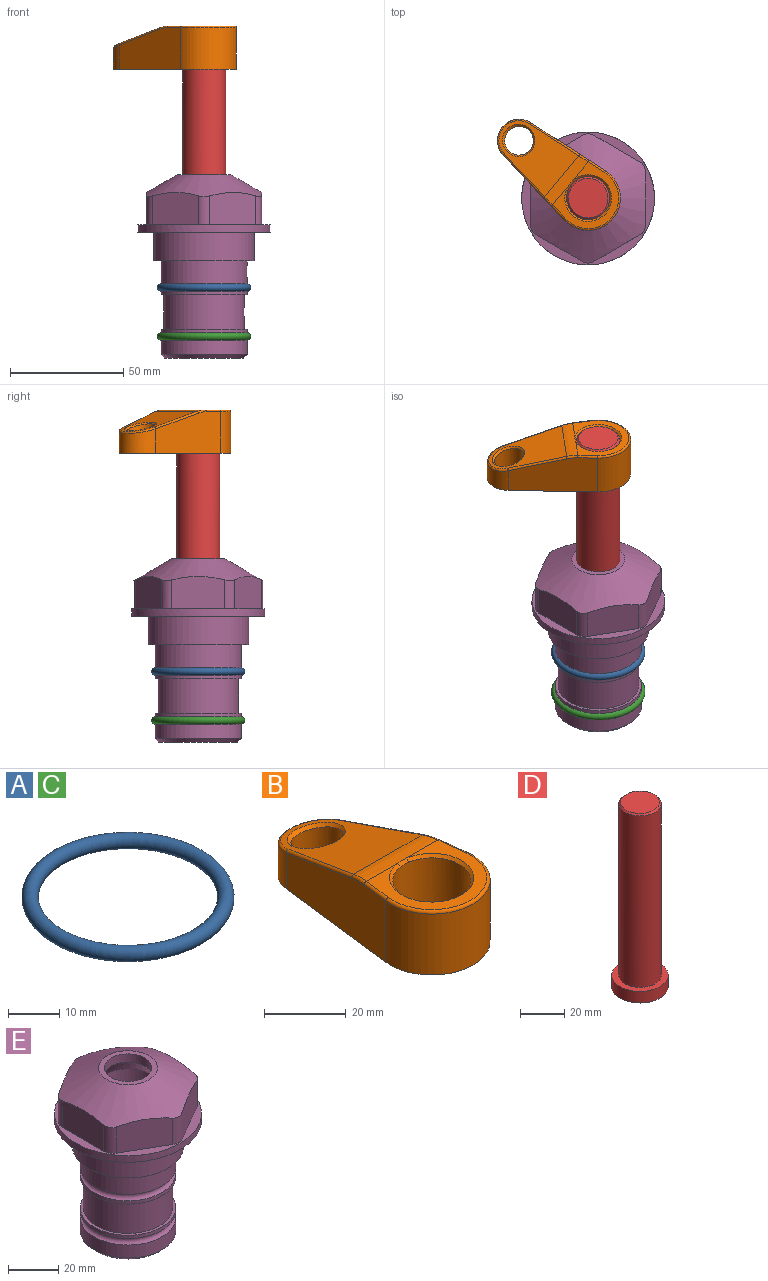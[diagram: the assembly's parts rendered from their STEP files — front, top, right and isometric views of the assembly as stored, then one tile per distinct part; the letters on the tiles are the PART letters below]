
ASSEMBLY  parts=5 mates=4
PART A: 1 faces, bbox 44.7x44.7x3.2 mm
  f0: torus R=19.05mm, axis (0,0,1), area 1193.9mm2
PART B: 31 faces, bbox 31.7x65.5x19.8 mm
  f0: plane 39.12x18.26mm, normal (0.99,0.12,0), area 612.2mm2, adj f1,f4,f7,f11,f13,f15
  f1: cylinder r=9.53mm len=18.91mm, axis (0,0,-1), area 296.1mm2, adj f0,f2,f7,f17
  f2: plane 39.12x18.26mm, normal (-0.99,0.12,0), area 612.2mm2, adj f1,f4,f7,f12,f14,f16
  f3: cylinder r=6.35mm len=12.7mm, axis (0,0,-1), area 362.4mm2, adj f7,f18
  f4: cylinder r=14.29mm len=28.58mm, axis (0,0,-1), area 882.2mm2, adj f0,f2,f7,f10
  f5: cylinder r=9.53mm len=19.05mm, axis (0,0,-1), area 1092.6mm2, adj f7,f19,f20
  f6: plane 26.99x23.69mm, normal (0,0,1), area 216.2mm2, adj f9,f10,f11,f12,f19
  f7: plane 63.5x28.58mm, normal (0,0,-1), area 661.8mm2, adj f0,f1,f2,f3,f4,f5,f22,f23
  f8: plane 33.52x23.6mm, normal (0,0.26,0.97), area 486mm2, adj f9,f15,f16,f17,f18
  f9: cylinder r=19.05mm len=24.72mm, axis (1,0,0), area 120.4mm2, adj f6,f8,f13,f14,f20
  f10: torus R=13.49mm, axis (0,0,1), area 59mm2, adj f4,f6,f11,f12
  f11: cylinder r=0.79mm len=8.67mm, axis (0.12,-0.99,0), area 10.8mm2, adj f0,f6,f10,f13
  f12: cylinder r=0.79mm len=8.67mm, axis (0.12,0.99,0), area 10.8mm2, adj f2,f6,f10,f14
  f13: bspline ~4.95x1.42mm, area 6.1mm2, adj f0,f9,f11,f15
  f14: bspline ~4.95x1.42mm, area 6.1mm2, adj f2,f9,f12,f16
  f15: cylinder r=0.79mm len=25.95mm, axis (0.12,-0.96,0.26), area 32.9mm2, adj f0,f8,f13,f17
  f16: cylinder r=0.79mm len=25.95mm, axis (0.12,0.96,-0.26), area 32.9mm2, adj f2,f8,f14,f17
  f17: bspline ~18.91x8.38mm, area 30mm2, adj f1,f8,f15,f16
  f18: bspline ~14.29x14.29mm, area 48.3mm2, adj f3,f8
  f19: cone r=9.53mm half-angle=45deg, axis (0,0,1), area 66.5mm2, adj f5,f6,f20
  f20: bspline ~3.22x0.96mm, area 3.5mm2, adj f5,f9,f19
  f21: plane 2.75x2.72mm, normal (0,0,-1), area 2.9mm2, adj f23,f25,f28
  f22: plane 23.05x15.88mm, normal (-0.99,-0.12,0), area 323.6mm2, adj f7,f25,f26,f27,f28,f29
  f23: plane 23.05x15.88mm, normal (0.99,-0.12,0), area 323.6mm2, adj f7,f21,f25,f27,f28,f30
  f24: cylinder r=9.53mm len=10.69mm, axis (0,0,-1), area 114.7mm2, adj f7,f27,f29,f30
  f25: cylinder r=12.7mm len=20.59mm, axis (0,0,-1), area 381.1mm2, adj f7,f21,f22,f23,f26,f28
  f26: plane 2.75x2.72mm, normal (0,0,-1), area 2.9mm2, adj f22,f25,f28
  f27: plane 19.72x18.37mm, normal (0,-0.26,-0.97), area 291.8mm2, adj f22,f23,f24,f28,f29,f30
  f28: cylinder r=15.88mm len=19.92mm, axis (1,0,0), area 54.8mm2, adj f21,f22,f23,f25,f26,f27
  f29: cylinder r=1.59mm len=11mm, axis (0,0,-1), area 34.7mm2, adj f7,f22,f24,f27
  f30: cylinder r=1.59mm len=11mm, axis (0,0,-1), area 34.7mm2, adj f7,f23,f24,f27
PART C: same geometry as A
PART D: 6 faces, bbox 25.4x25.4x101.6 mm
  f0: plane 17.46x17.46mm, normal (0,0,1), area 239.5mm2, adj f5
  f1: plane 25.4x25.4mm, normal (0,0,-1), area 506.7mm2, adj f2
  f2: cylinder r=12.7mm len=25.4mm, axis (0,0,1), area 506.7mm2, adj f1,f3
  f3: plane 25.4x25.4mm, normal (0,0,1), area 221.7mm2, adj f2,f4
  f4: cylinder r=9.53mm len=94.46mm, axis (0,0,1), area 5653mm2, adj f3,f5
  f5: cone r=8.73mm half-angle=45deg, axis (0,0,-1), area 64.4mm2, adj f0,f4
PART E: 36 faces, bbox 58.7x58.7x81 mm
  f0: cylinder r=17.78mm len=35.56mm, axis (0,0,1), area 1670.8mm2, adj f23,f24,f31
  f1: cylinder r=19.05mm len=38.1mm, axis (0,0,1), area 1191.9mm2, adj f26,f27,f30
  f2: plane 58.66x58.66mm, normal (0,0,-1), area 1150.6mm2, adj f3,f28
  f3: cylinder r=29.33mm len=58.66mm, axis (0,0,-1), area 585.1mm2, adj f2,f4
  f4: plane 58.66x58.66mm, normal (0,0,1), area 475.9mm2, adj f3,f5,f6,f7,f8,f9,f10,f11
  f5: plane 20.32x14.34mm, normal (-0.5,0.87,0), area 324.4mm2, adj f4,f15,f16,f17
  f6: plane 20.32x14.34mm, normal (0.5,0.87,0), area 324.4mm2, adj f4,f14,f15,f17
  f7: plane 23.48x14.34mm, normal (1,0,0), area 324.4mm2, adj f4,f13,f14,f17
  f8: plane 20.32x14.34mm, normal (0.5,-0.87,0), area 324.4mm2, adj f4,f12,f13,f17
  f9: plane 20.32x14.34mm, normal (-0.5,-0.87,0), area 324.4mm2, adj f4,f11,f12,f17
  f10: plane 23.48x14.34mm, normal (-1,0,0), area 324.4mm2, adj f4,f11,f16,f17
  f11: cylinder r=5.08mm len=12.85mm, axis (0,0,-1), area 67.2mm2, adj f4,f9,f10,f17
  f12: cylinder r=5.08mm len=12.85mm, axis (0,0,-1), area 67.2mm2, adj f4,f8,f9,f17
  f13: cylinder r=5.08mm len=12.85mm, axis (0,0,-1), area 67.2mm2, adj f4,f7,f8,f17
  f14: cylinder r=5.08mm len=12.85mm, axis (0,0,-1), area 67.2mm2, adj f4,f6,f7,f17
  f15: cylinder r=5.08mm len=12.85mm, axis (0,0,-1), area 67.2mm2, adj f4,f5,f6,f17
  f16: cylinder r=5.08mm len=12.85mm, axis (0,0,-1), area 67.2mm2, adj f4,f5,f10,f17
  f17: cone r=11.73mm half-angle=60deg, axis (0,0,-1), area 2071.8mm2, adj f5,f6,f7,f8,f9,f10,f11,f12
  f18: plane 23.46x23.46mm, normal (0,0,1), area 147.4mm2, adj f17,f35
  f19: plane 34.93x34.93mm, normal (0,0,-1), area 958mm2, adj f29
  f20: cylinder r=19.05mm len=38.1mm, axis (0,0,1), area 760.1mm2, adj f21,f29
  f21: torus R=19.05mm, axis (0,0,1), area 565.3mm2, adj f20,f22
  f22: cylinder r=19.05mm len=38.1mm, axis (0,0,1), area 190mm2, adj f21,f23
  f23: plane 38.1x38.1mm, normal (0,0,1), area 146.9mm2, adj f0,f22
  f24: plane 38.1x38.1mm, normal (0,0,-1), area 146.9mm2, adj f0,f25
  f25: cylinder r=19.05mm len=38.1mm, axis (0,0,1), area 190mm2, adj f24,f26
  f26: torus R=19.05mm, axis (0,0,1), area 565.3mm2, adj f1,f25
  f27: plane 44.45x44.45mm, normal (0,0,-1), area 411.7mm2, adj f1,f28
  f28: cylinder r=22.23mm len=44.45mm, axis (0,0,1), area 1773.5mm2, adj f2,f27
  f29: cone r=19.05mm half-angle=45deg, axis (0,0,1), area 257.5mm2, adj f19,f20
  f30: cylinder r=3.17mm len=6.75mm, axis (-1,0,0), area 128mm2, adj f1,f33
  f31: cylinder r=3.17mm len=6.35mm, axis (-1,0,0), area 102.5mm2, adj f0,f33
  f32: plane 25.4x25.4mm, normal (0,0,1), area 506.7mm2, adj f33
  f33: cylinder r=12.7mm len=66.42mm, axis (0,0,-1), area 5236.2mm2, adj f30,f31,f32,f34
  f34: cone r=9.53mm half-angle=30deg, axis (0,0,-1), area 443.4mm2, adj f33,f35
  f35: cylinder r=9.53mm len=19.05mm, axis (0,0,-1), area 240.9mm2, adj f18,f34
PLACE A at identity
PLACE B rot(axis=(0,0,1),50.3deg) t=(0,0,27.55)mm
PLACE C t=(0,0,-21.59)mm
PLACE D rot(axis=(0,0,1),50.3deg) t=(0,0,27.55)mm
PLACE E at identity fixed
MATE cylindrical D.f2 <-> E.f0  axis (0,0,-1) through (0,0,-10.55)mm
MATE fastened A.f0 <-> E.f0  axis (0,0,1) through (0,0,-24.51)mm
MATE fastened C.f0 <-> E.f0  axis (0,0,1) through (0,0,-46.1)mm
MATE fastened D.f2 <-> B.f4  axis (0,0,1) through (0,0,91.05)mm
